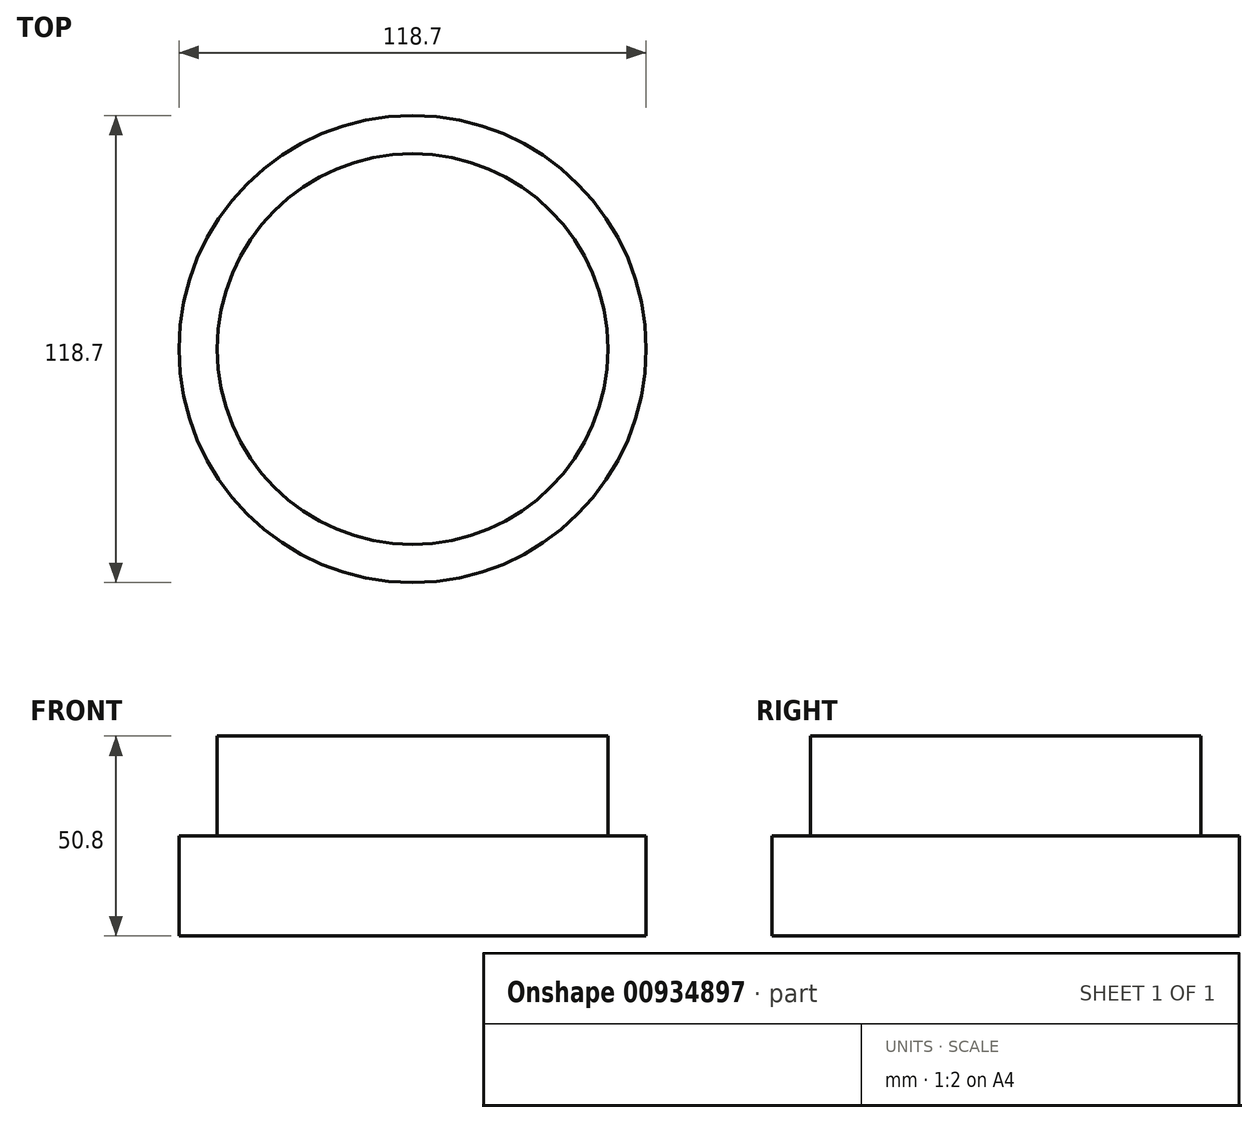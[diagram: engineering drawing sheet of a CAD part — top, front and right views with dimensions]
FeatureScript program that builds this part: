
annotation { "Feature Type Name" : "Feature", "Feature Type Description" : "" }
export const myFeature = defineFeature(function(context is Context, id is Id, definition is map)
    precondition{}
    {
        {
            var Q0;
            Q0=qCreatedBy(makeId("Top.planeOp"),FACE);
            var sketch = newSketch(context, id + "F0", { "sketchPlane" : qUnion([Q0])});
            skCircle(sketch, "E0", {"center": v(0, 0) * mm, "radius": 59.35 * mm});
            skSolve(sketch);
        }
        {
            var Q0;
            Q0=makeQuery(id+"F0.imprint","IMPRINT",FACE,{"disambiguationData":[TD([[makeQuery(id+"F0.imprint","IMPRINT",EDGE,{"derivedFrom":sQuery(id+"F0.wireOp",EDGE,"E0")}),1.0]])]});
            var Q1;
            Q1=sQuery(id+"F0.wireOp",EDGE,"E0");
            extrude(context, id + "F1", {"entities" : qUnion([Q0]), "surfaceEntities" : qUnion([Q1]), "depth" : 25.4 * mm, "offsetDistance" : 25.4 * mm});
        }
        {
            var Q0;
            Q0=makeQuery(id+"F1.opExtrude","CAP_FACE",FACE,{"disambiguationData":[OSD([sQuery(id+"F0.wireOp",EDGE,"E0")])],"isStart":false});
            var sketch = newSketch(context, id + "F2", { "sketchPlane" : qUnion([Q0])});
            skCircle(sketch, "E1", {"center": v(0, 0) * mm, "radius": 49.65 * mm});
            skSolve(sketch);
        }
        {
            var Q0;
            Q0 = qSketchRegion(id + "F2", true);
            var Q1;
            Q1=makeQuery(id+"F2.imprint","IMPRINT",FACE,{"disambiguationData":[TD([[makeQuery(id+"F2.imprint","IMPRINT",EDGE,{"derivedFrom":sQuery(id+"F2.wireOp",EDGE,"E1")}),1.0]])]});
            extrude(context, id + "F3", {"entities" : qUnion([Q0, Q1]), "operationType" : NewBodyOperationType.ADD, "depth" : 25.4 * mm, "offsetDistance" : 25.4 * mm});
        }
    });
